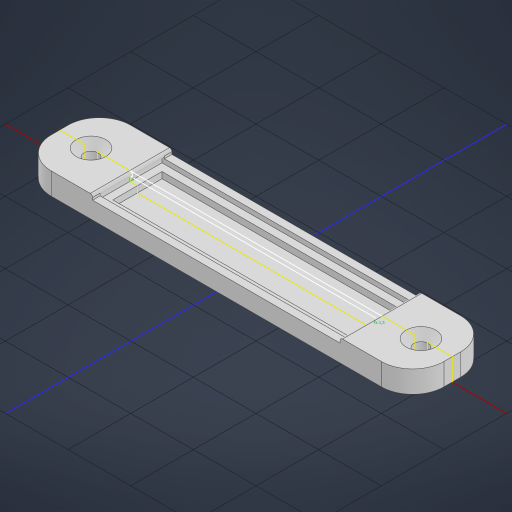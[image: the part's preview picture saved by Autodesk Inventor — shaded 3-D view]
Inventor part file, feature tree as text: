
AUTODESK INVENTOR PART (.ipt)
format: ipt  version: 2023.2 (Build 272271030, 271C)  size: 282,624 bytes
history: native  units: mm
features: extrude x5, sketch x3, hole x1, other x1
ambient origin geometry x8: Origin, YZ Plane, XZ Plane, XY Plane, X Axis, Y Axis, Z Axis, Center Point
bodies: Volumenkörper1 (feature_tree)
feature tree (10):
  sketch  "Skizze1"  dims[d0=80.5mm d1=20.5mm]
  extrude  "Extrusion1"  Depth=20.5mm
  extrude  "Extrusion2"  Depth=2.4mm
  extrude  "Extrusion3"  Depth=4.0mm
  sketch  "Skizze2"  dims[d2=2.4mm d3=2.4mm]
  extrude  "Extrusion4"  Depth=2.0mm TaperAngle=0.0deg
  hole  "Bohrung1"  [1 undecoded]
  extrude  "Extrusion5"  Depth=2.0mm TaperAngle=0.0deg
  sketch  "Skizze3"  dims[d4=4.0mm d7=4.0mm d8=2.0mm d9=0.0mm d10=5.0mm d11=0.0mm d12=2.0mm d13=0.0mm d14=1.5mm d15=1.5mm d16=20.5mm d17=0.0mm d18=4.5mm d19=6.0mm d20=9.4mm d21=2.0mm d22=90.0deg d23=6.0mm d24=0.0mm d25=20.0mm d26=10.0mm d27=10.0mm d28=20.0mm d29=10.0mm d30=10.0mm d31=0.0mm d32=0.0mm]
  other  "Schnittkanten projizieren1"
note: 1 required parameter value undecoded (feature->parameter linkage not recoverable at this tier; creation-order binding heuristic only, values carry confidence <= 0.55)
